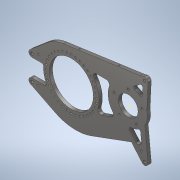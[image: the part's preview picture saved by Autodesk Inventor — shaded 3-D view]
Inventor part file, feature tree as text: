
AUTODESK INVENTOR PART (.ipt)
format: ipt  version: 2021 (Build 250183000, 183)  size: 532,992 bytes
history: native  units: in
note: dims shown in document units (in); Inventor stores cm internally (conversion verified against a paired STEP export)
features: sketch x16, extrude x12, fillet x7, hole x5, chamfer x1, projected_geometry x1
ambient origin geometry x8: Origin, YZ Plane, XZ Plane, XY Plane, X Axis, Y Axis, Z Axis, Center Point
bodies: Body1 (feature_tree)
feature tree (42):
  extrude  "Extrusion13"  Depth=0.5in TaperAngle=0.0deg
  hole  "Hole4"  [1 undecoded]
  extrude  "Extrusion15"  Depth=1.0in
  extrude  "Extrusion17"  Depth=0.5in TaperAngle=0.0deg
  hole  "Hole9"  [1 undecoded]
  hole  "Hole10"  [1 undecoded]
  extrude  "Extrusion18"  Depth=1.0in
  extrude  "Extrusion19"  Depth=0.239in
  extrude  "Extrusion24"  Depth=0.5in
  fillet  "Fillet3"  Radius=0.1718in
  extrude  "Extrusion27"  Depth=0.75in
  chamfer  "Chamfer1"  Distance=1.0in
  sketch  "Sketch40"  dims[d194=0.3526in d197=0.239in]
  extrude  "Extrusion29"  Depth=0.25in
  extrude  "Extrusion30"  Depth=0.5in TaperAngle=0.0deg
  fillet  "Fillet4"  Radius=0.75in
  fillet  "Fillet5"  Radius=1.0in
  extrude  "Extrusion32"  Depth=0.75in
  extrude  "Extrusion35"  Depth=0.75in
  fillet  "Fillet6"  Radius=0.5in
  fillet  "Fillet7"  Radius=2.8in
  extrude  "Extrusion36"  Depth=0.25in
  fillet  "Fillet8"  Radius=0.5in
  hole  "Hole12"  [1 undecoded]
  hole  "Hole14"  [1 undecoded]
  fillet  "Fillet9"  Radius=1.0in
  sketch  "Sketch14"  dims[d96=8.5in d97=2.16in d98=9.0in d99=5.5in d100=1.0in d101=1.0in d102=6.0in d103=6.0in d104=3.718in d105=1.0in d108=10.718in d109=1.5in d111=0.5in d112=0.0in]
  sketch  "Sketch15"  dims[d113=0.386in d114=0.75in d115=0.762in d116=0.25in d117=0.5635in d118=0.484in d119=0.8108in d132=5.0in]
  sketch  "Sketch18"  dims[d133=17.223in d134=1.0in]
  sketch  "Sketch21"  dims[d135=1.0in d136=0.5in d137=0.0in]
  sketch  "Sketch29"  dims[d155=1.0in d156=0.0in d178=7.75in]
  sketch  "Sketch31"  dims[d179=3.5433in d181=360.0deg]
  sketch  "Sketch32"  dims[d183=0.257in d184=0.75in d185=0.438in d186=0.25in d187=0.5635in d188=1.0in d189=0.8108in d191=1.0in]
  sketch  "Sketch39"  dims[d192=0.0481in d193=1.0in]
  sketch  "Sketch42"  dims[d198=0.1195in d199=0.5in]
  sketch  "Sketch43"  dims[d200=0.266in d201=0.75in d202=0.507in d203=0.25in d204=0.5635in d205=1.0in d206=0.8108in d207=0.1718in]
  sketch  "Sketch45"  dims[d208=15.0deg d210=0.75in]
  sketch  "Sketch48"  dims[d211=0.75in]
  sketch  "Sketch49"  dims[d212=0.75in]
  sketch  "Sketch51"  dims[d213=0.25in]
  sketch  "Sketch54"  dims[d214=0.5in d215=1.0in d216=0.0in d217=0.25in d218=1.0in d219=0.0in d223=0.75in d242=1.0in d243=0.0in d247=0.75in d249=0.75in d250=0.5in d251=2.8in d262=0.25in d263=0.5in d264=1.0in d265=0.0in d266=0.0156in d267=0.125in d268=45.0deg d284=1.0in d285=0.0in d296=6.75in d297=1.0in d298=0.0in d303=3.005in d304=8.715in d305=6.5in d306=0.5in d307=0.5in d308=4.44in d309=0.325in d310=1.9685in d312=360.0deg d314=1.0in d315=0.0in d317=0.061in d332=0.055in d333=0.5in d334=0.0in d335=11.5in d336=5.0in d337=3.0in d339=0.5in d340=0.0in d341=7.0in d353=2.25in d354=8.375in d355=0.25in d356=0.196in d357=0.5in d358=0.375in d359=0.25in d360=0.5635in d361=0.65in d362=0.8108in d370=0.25in d371=1.75in d372=0.196in d373=0.5in d374=0.375in d375=0.25in d376=0.5635in d377=0.65in d378=0.8108in d379=3.0in d381=6.4in d382=0.25in d383=0.0069in d283=0.5in d286=0.0344in]
  projected_geometry  "Project Cut Edges1"
note: 5 required parameter values undecoded (feature->parameter linkage not recoverable at this tier; creation-order binding heuristic only, values carry confidence <= 0.55)
